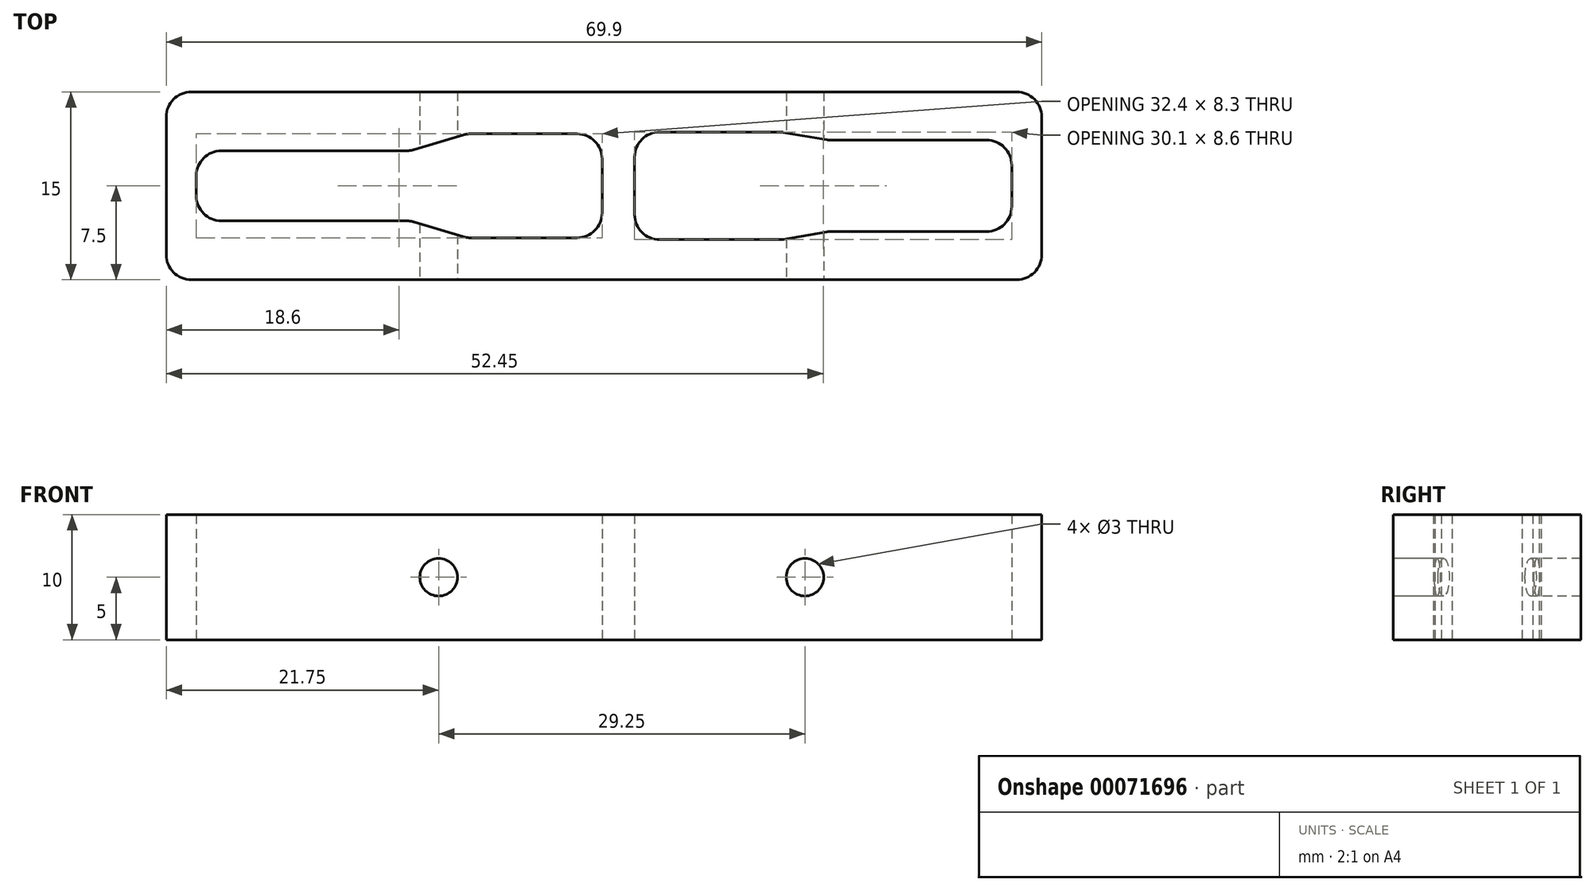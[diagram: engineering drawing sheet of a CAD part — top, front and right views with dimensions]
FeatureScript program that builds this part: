
annotation { "Feature Type Name" : "Feature", "Feature Type Description" : "" }
export const myFeature = defineFeature(function(context is Context, id is Id, definition is map)
    precondition{}
    {
        {
            var Q0;
            Q0=qCreatedBy(makeId("Top.planeOp"),FACE);
            var sketch = newSketch(context, id + "F0", { "sketchPlane" : qUnion([Q0])});
            skLineSegment(sketch, "E0.rect.bottom", {"start": v(34.95, -7.5) * mm, "end": v(-34.95, -7.5) * mm});
            skLineSegment(sketch, "E0.rect.top", {"start": v(34.95, 7.5) * mm, "end": v(-34.95, 7.5) * mm});
            skLineSegment(sketch, "E0.rect.left", {"start": v(34.95, -7.5) * mm, "end": v(34.95, 7.5) * mm});
            skLineSegment(sketch, "E0.rect.right", {"start": v(-34.95, -7.5) * mm, "end": v(-34.95, 7.5) * mm});
            skPoint(sketch, "E0.rect.middle", {"position": v(0, 0) * mm});
            skLineSegment(sketch, "E1.rect.bottom", {"start": v(-15.45, -2.8) * mm, "end": v(-32.55, -2.8) * mm});
            skLineSegment(sketch, "E1.rect.top", {"start": v(-15.45, 2.8) * mm, "end": v(-32.55, 2.8) * mm});
            skLineSegment(sketch, "E1.rect.right", {"start": v(-32.55, -2.8) * mm, "end": v(-32.55, 2.8) * mm});
            skPoint(sketch, "E1.rect.middle", {"position": v(-24, 0) * mm});
            skLineSegment(sketch, "E2.rect.bottom", {"start": v(-0.15, -4.15) * mm, "end": v(-10.95, -4.15) * mm});
            skLineSegment(sketch, "E2.rect.top", {"start": v(-0.15, 4.15) * mm, "end": v(-10.95, 4.15) * mm});
            skPoint(sketch, "E2.rect.middle", {"position": v(-5.55, 0) * mm});
            skLineSegment(sketch, "E3.rect.bottom", {"start": v(14.15, -4.3) * mm, "end": v(2.45, -4.3) * mm});
            skLineSegment(sketch, "E3.rect.top", {"start": v(14.15, 4.3) * mm, "end": v(2.45, 4.3) * mm});
            skPoint(sketch, "E3.rect.middle", {"position": v(8.3, 0) * mm});
            skLineSegment(sketch, "E4.rect.bottom", {"start": v(32.55, -3.65) * mm, "end": v(17.95, -3.65) * mm});
            skLineSegment(sketch, "E4.rect.top", {"start": v(32.55, 3.65) * mm, "end": v(17.95, 3.65) * mm});
            skLineSegment(sketch, "E4.rect.left", {"start": v(32.55, -3.65) * mm, "end": v(32.55, 3.65) * mm});
            skPoint(sketch, "E4.rect.middle", {"position": v(25.25, 0) * mm});
            skLineSegment(sketch, "E5", {"start": v(-15.45, 2.8) * mm, "end": v(-10.95, 4.15) * mm});
            skLineSegment(sketch, "E6", {"start": v(14.15, 4.3) * mm, "end": v(17.95, 3.65) * mm});
            skLineSegment(sketch, "E7", {"start": v(17.95, -3.65) * mm, "end": v(14.15, -4.3) * mm});
            skLineSegment(sketch, "E8", {"start": v(-10.95, -4.15) * mm, "end": v(-15.45, -2.8) * mm});
            skLineSegment(sketch, "E9", {"start": v(-0.15, 4.15) * mm, "end": v(-0.15, -4.15) * mm});
            skLineSegment(sketch, "E10", {"start": v(2.45, -4.3) * mm, "end": v(2.45, 4.3) * mm});
            skSolve(sketch);
        }
        {
            var Q0;
            Q0 = qSketchRegion(id + "F0", true);
            extrude(context, id + "F1", {"entities" : qUnion([Q0]), "endBound" : BoundingType.SYMMETRIC, "depth" : 10 * mm});
        }
        {
            var Q0;
            Q0=qCreatedBy(makeId("Front.planeOp"),FACE);
            var sketch = newSketch(context, id + "F2", { "sketchPlane" : qUnion([Q0])});
            skLineSegment(sketch, "E11.0", {"start": v(-15.45, 5) * mm, "end": v(-15.45, -5) * mm, "construction": true});
            skLineSegment(sketch, "E12.0", {"start": v(-10.95, 5) * mm, "end": v(-10.95, -5) * mm, "construction": true});
            skLineSegment(sketch, "E13.0", {"start": v(14.15, 5) * mm, "end": v(14.15, -5) * mm, "construction": true});
            skLineSegment(sketch, "E14.0", {"start": v(17.95, 5) * mm, "end": v(17.95, -5) * mm, "construction": true});
            skLineSegment(sketch, "E15", {"start": v(-15.45, -5) * mm, "end": v(-10.95, 5) * mm, "construction": true});
            skLineSegment(sketch, "E16", {"start": v(14.15, -5) * mm, "end": v(17.95, 5) * mm, "construction": true});
            skCircle(sketch, "E17", {"center": v(-13.2, 0) * mm, "radius": 1.5 * mm});
            skCircle(sketch, "E18", {"center": v(16.05, 0) * mm, "radius": 1.5 * mm});
            skSolve(sketch);
        }
        {
            var Q0;
            Q0 = qSketchRegion(id + "F2", true);
            extrude(context, id + "F3", {"entities" : qUnion([Q0]), "operationType" : NewBodyOperationType.REMOVE, "endBound" : BoundingType.SYMMETRIC, "oppositeDirection" : true, "depth" : 25 * mm});
        }
        {
            var Q0;
            Q0=makeQuery(id+"F1.opExtrude","SWEPT_EDGE",EDGE,{"disambiguationData":[OSD([sQuery(id+"F0.wireOp",EDGE,"E0.rect.top"),sQuery(id+"F0.wireOp",EDGE,"E0.rect.right")])]});
            var Q1;
            Q1=makeQuery(id+"F1.opExtrude","SWEPT_EDGE",EDGE,{"disambiguationData":[OSD([sQuery(id+"F0.wireOp",EDGE,"E0.rect.bottom"),sQuery(id+"F0.wireOp",EDGE,"E0.rect.right")])]});
            var Q2;
            Q2=makeQuery(id+"F1.opExtrude","SWEPT_EDGE",EDGE,{"disambiguationData":[OSD([sQuery(id+"F0.wireOp",EDGE,"E0.rect.bottom"),sQuery(id+"F0.wireOp",EDGE,"E0.rect.left")])]});
            var Q3;
            Q3=makeQuery(id+"F1.opExtrude","SWEPT_EDGE",EDGE,{"disambiguationData":[OSD([sQuery(id+"F0.wireOp",EDGE,"E0.rect.top"),sQuery(id+"F0.wireOp",EDGE,"E0.rect.left")])]});
            fillet(context, id + "F4", {"entities" : qUnion([Q0, Q1, Q2, Q3]), "radius" : 2 * mm, "tangentPropagation" : true, "allowEdgeOverflow" : false});
        }
        {
            var Q0;
            Q0=makeQuery(id+"F1.opExtrude","SWEPT_EDGE",EDGE,{"disambiguationData":[OSD([sQuery(id+"F0.wireOp",EDGE,"E1.rect.top"),sQuery(id+"F0.wireOp",EDGE,"E1.rect.right")])]});
            var Q1;
            Q1=makeQuery(id+"F1.opExtrude","SWEPT_EDGE",EDGE,{"disambiguationData":[OSD([sQuery(id+"F0.wireOp",EDGE,"E4.rect.top"),sQuery(id+"F0.wireOp",EDGE,"E4.rect.left")])]});
            var Q2;
            Q2=makeQuery(id+"F1.opExtrude","SWEPT_EDGE",EDGE,{"disambiguationData":[OSD([sQuery(id+"F0.wireOp",EDGE,"E4.rect.bottom"),sQuery(id+"F0.wireOp",EDGE,"E4.rect.left")])]});
            var Q3;
            Q3=makeQuery(id+"F1.opExtrude","SWEPT_EDGE",EDGE,{"disambiguationData":[OSD([sQuery(id+"F0.wireOp",EDGE,"E1.rect.bottom"),sQuery(id+"F0.wireOp",EDGE,"E1.rect.right")])]});
            var Q4;
            Q4=makeQuery(id+"F1.opExtrude","SWEPT_EDGE",EDGE,{"disambiguationData":[OSD([sQuery(id+"F0.wireOp",EDGE,"E1.rect.top"),sQuery(id+"F0.wireOp",EDGE,"E5")])]});
            var Q5;
            Q5=makeQuery(id+"F1.opExtrude","SWEPT_EDGE",EDGE,{"disambiguationData":[OSD([sQuery(id+"F0.wireOp",EDGE,"E2.rect.top"),sQuery(id+"F0.wireOp",EDGE,"E5")])]});
            var Q6;
            Q6=makeQuery(id+"F1.opExtrude","SWEPT_EDGE",EDGE,{"disambiguationData":[OSD([sQuery(id+"F0.wireOp",EDGE,"E3.rect.top"),sQuery(id+"F0.wireOp",EDGE,"s0bDXPDY-ctDG-qjSh-qIcy-iR2ZqsnkHCUU")])]});
            var Q7;
            Q7=makeQuery(id+"F1.opExtrude","SWEPT_EDGE",EDGE,{"disambiguationData":[OSD([sQuery(id+"F0.wireOp",EDGE,"E2.rect.top"),sQuery(id+"F0.wireOp",EDGE,"s0bDXPDY-ctDG-qjSh-qIcy-iR2ZqsnkHCUU")])]});
            var Q8;
            Q8=makeQuery(id+"F1.opExtrude","SWEPT_EDGE",EDGE,{"disambiguationData":[OSD([sQuery(id+"F0.wireOp",EDGE,"E3.rect.top"),sQuery(id+"F0.wireOp",EDGE,"E6")])]});
            var Q9;
            Q9=makeQuery(id+"F1.opExtrude","SWEPT_EDGE",EDGE,{"disambiguationData":[OSD([sQuery(id+"F0.wireOp",EDGE,"E4.rect.top"),sQuery(id+"F0.wireOp",EDGE,"E6")])]});
            var Q10;
            Q10=makeQuery(id+"F1.opExtrude","SWEPT_EDGE",EDGE,{"disambiguationData":[OSD([sQuery(id+"F0.wireOp",EDGE,"E1.rect.bottom"),sQuery(id+"F0.wireOp",EDGE,"E8")])]});
            var Q11;
            Q11=makeQuery(id+"F1.opExtrude","SWEPT_EDGE",EDGE,{"disambiguationData":[OSD([sQuery(id+"F0.wireOp",EDGE,"E2.rect.bottom"),sQuery(id+"F0.wireOp",EDGE,"E8")])]});
            var Q12;
            Q12=makeQuery(id+"F1.opExtrude","SWEPT_EDGE",EDGE,{"disambiguationData":[OSD([sQuery(id+"F0.wireOp",EDGE,"E2.rect.bottom"),sQuery(id+"F0.wireOp",EDGE,"Bh5gwCBw-FpQK-04Ta-b9JR-4ePIGMfl4smV")])]});
            var Q13;
            Q13=makeQuery(id+"F1.opExtrude","SWEPT_EDGE",EDGE,{"disambiguationData":[OSD([sQuery(id+"F0.wireOp",EDGE,"E3.rect.bottom"),sQuery(id+"F0.wireOp",EDGE,"Bh5gwCBw-FpQK-04Ta-b9JR-4ePIGMfl4smV")])]});
            var Q14;
            Q14=makeQuery(id+"F1.opExtrude","SWEPT_EDGE",EDGE,{"disambiguationData":[OSD([sQuery(id+"F0.wireOp",EDGE,"E3.rect.bottom"),sQuery(id+"F0.wireOp",EDGE,"E7")])]});
            var Q15;
            Q15=makeQuery(id+"F1.opExtrude","SWEPT_EDGE",EDGE,{"disambiguationData":[OSD([sQuery(id+"F0.wireOp",EDGE,"E4.rect.bottom"),sQuery(id+"F0.wireOp",EDGE,"E7")])]});
            fillet(context, id + "F5", {"entities" : qUnion([Q0, Q1, Q2, Q3, Q4, Q5, Q6, Q7, Q8, Q9, Q10, Q11, Q12, Q13, Q14, Q15]), "radius" : 2 * mm, "tangentPropagation" : true, "allowEdgeOverflow" : false});
        }
    });
